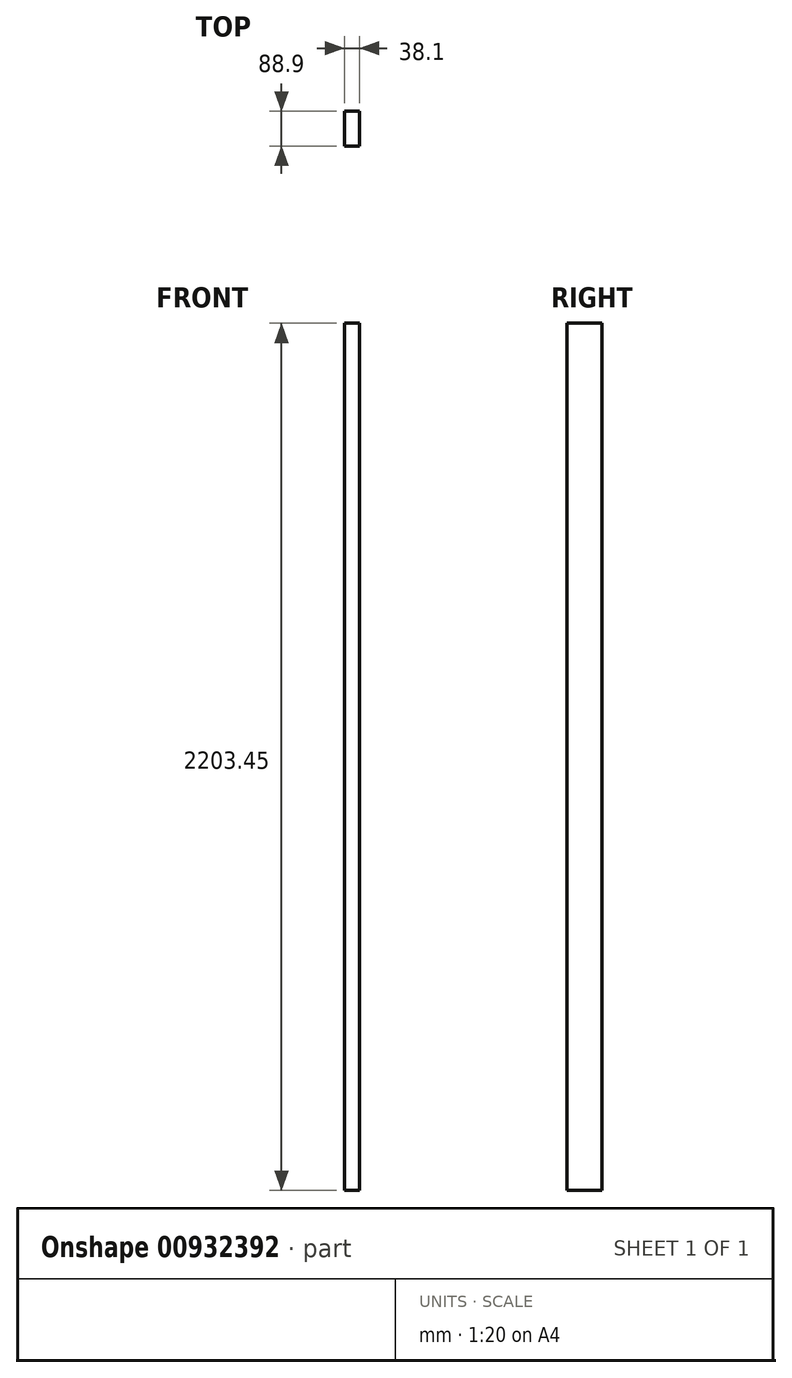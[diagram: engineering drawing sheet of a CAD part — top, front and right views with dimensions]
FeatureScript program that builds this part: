
annotation { "Feature Type Name" : "Feature", "Feature Type Description" : "" }
export const myFeature = defineFeature(function(context is Context, id is Id, definition is map)
    precondition{}
    {
        {
            var Q0;
            Q0=qCreatedBy(makeId("Top.planeOp"),FACE);
            var sketch = newSketch(context, id + "F0", { "sketchPlane" : qUnion([Q0])});
            skLineSegment(sketch, "E0.bottom", {"start": v(19.05, 44.45) * mm, "end": v(-19.05, 44.45) * mm});
            skLineSegment(sketch, "E0.top", {"start": v(19.05, -44.45) * mm, "end": v(-19.05, -44.45) * mm});
            skLineSegment(sketch, "E0.left", {"start": v(19.05, 44.45) * mm, "end": v(19.05, -44.45) * mm});
            skLineSegment(sketch, "E0.right", {"start": v(-19.05, 44.45) * mm, "end": v(-19.05, -44.45) * mm});
            skPoint(sketch, "E0.middle", {"position": v(0, 0) * mm});
            skSolve(sketch);
        }
        {
            var Q0;
            Q0=makeQuery(id+"F0.imprint","IMPRINT",FACE,{"disambiguationData":[TD([[makeQuery(id+"F0.imprint","IMPRINT",EDGE,{"derivedFrom":sQuery(id+"F0.wireOp",EDGE,"E0.bottom")}),1.0]])]});
            extrude(context, id + "F1", {"entities" : qUnion([Q0]), "depth" : 2203.45 * mm, "offsetDistance" : 25.4 * mm});
        }
    });
